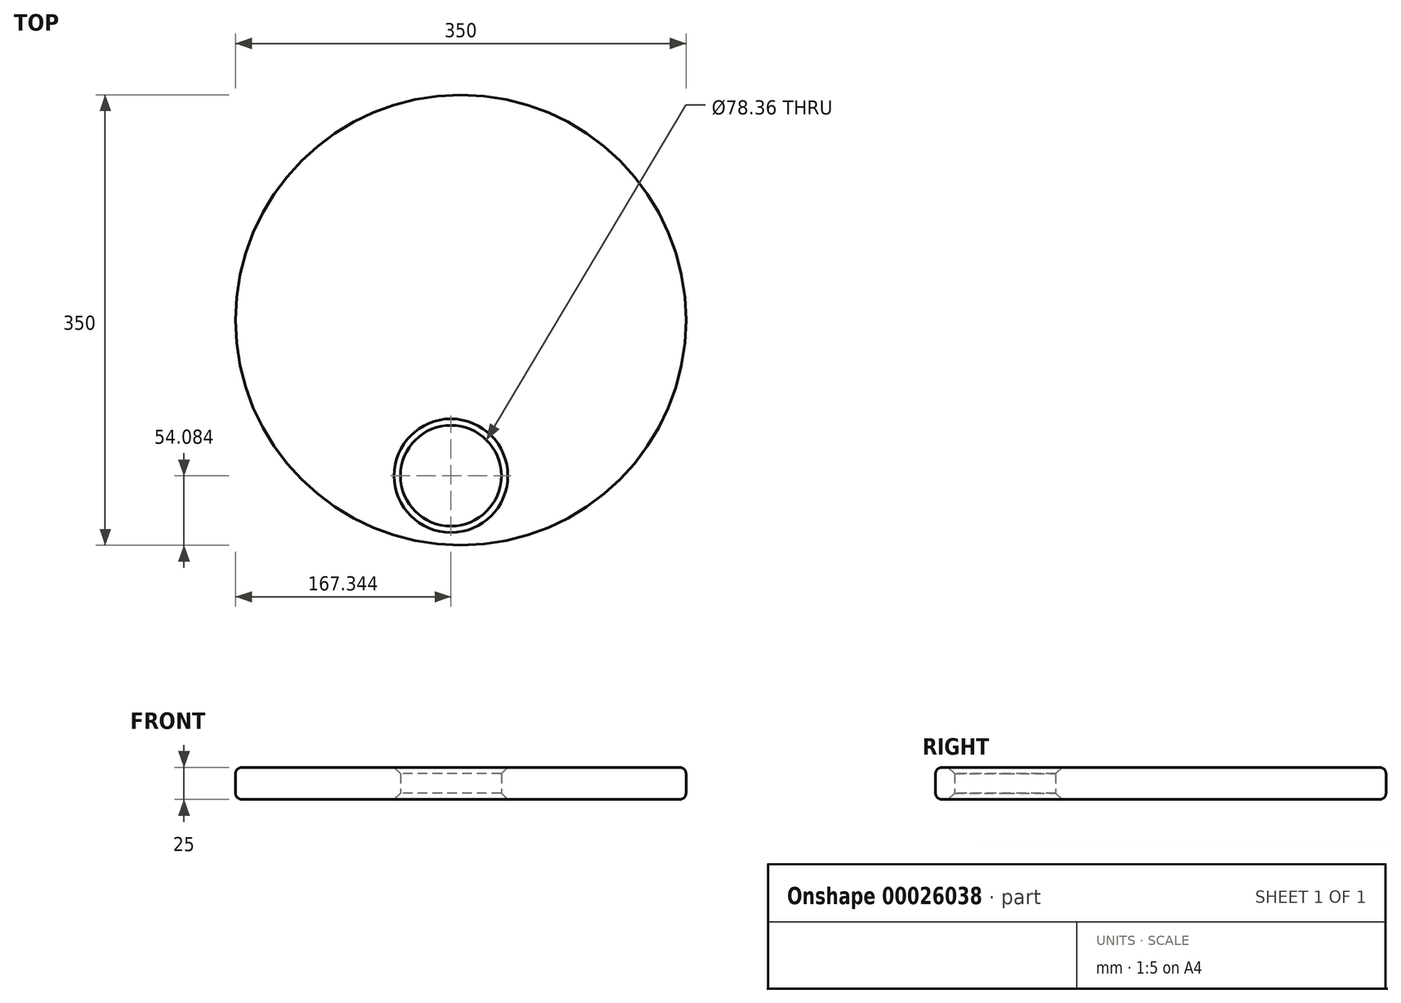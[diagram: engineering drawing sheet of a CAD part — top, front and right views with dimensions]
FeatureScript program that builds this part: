
annotation { "Feature Type Name" : "Feature", "Feature Type Description" : "" }
export const myFeature = defineFeature(function(context is Context, id is Id, definition is map)
    precondition{}
    {
        {
            var Q0;
            Q0=qCreatedBy(makeId("Top.planeOp"),FACE);
            var sketch = newSketch(context, id + "F0", { "sketchPlane" : qUnion([Q0])});
            skCircle(sketch, "E0", {"center": v(0, 0) * mm, "radius": 175 * mm});
            skSolve(sketch);
        }
        {
            var Q0;
            Q0 = qSketchRegion(id + "F0", true);
            extrude(context, id + "F1", {"entities" : qUnion([Q0]), "depth" : 25 * mm});
        }
        {
            var Q0;
            Q0=makeQuery(id+"F1.opExtrude","CAP_EDGE",EDGE,{"disambiguationData":[OSD([sQuery(id+"F0.wireOp",EDGE,"E0")])],"isStart":false});
            var Q1;
            Q1=makeQuery(id+"F1.opExtrude","CAP_EDGE",EDGE,{"disambiguationData":[OSD([sQuery(id+"F0.wireOp",EDGE,"E0")])],"isStart":true});
            fillet(context, id + "F2", {"entities" : qUnion([Q0, Q1]), "radius" : 5 * mm, "tangentPropagation" : true, "allowEdgeOverflow" : false});
        }
        {
            var Q0;
            Q0=makeQuery(id+"F1.opExtrude","CAP_FACE",FACE,{"disambiguationData":[OSD([sQuery(id+"F0.wireOp",EDGE,"E0")])],"isStart":true});
            var sketch = newSketch(context, id + "F3", { "sketchPlane" : qUnion([Q0])});
            skCircle(sketch, "E1", {"center": v(-7.66, 120.92) * mm, "radius": 39.18 * mm});
            skSolve(sketch);
        }
        {
            var Q0;
            Q0 = qSketchRegion(id + "F3", true);
            extrude(context, id + "F4", {"entities" : qUnion([Q0]), "operationType" : NewBodyOperationType.REMOVE, "endBound" : BoundingType.THROUGH_ALL, "oppositeDirection" : true, "depth" : 25 * mm});
        }
        {
            var Q0;
            Q0=makeQuery(id+"F4.boolean.opBoolean","COPY",FACE,{"derivedFrom":makeQuery(id+"F4.opExtrude","SWEPT_FACE",FACE,{"disambiguationData":[OSD([sQuery(id+"F3.wireOp",EDGE,"E1")])]})});
            chamfer(context, id + "F5", {"entities" : qUnion([Q0]), "width" : 5 * mm, "tangentPropagation" : true});
        }
    });
